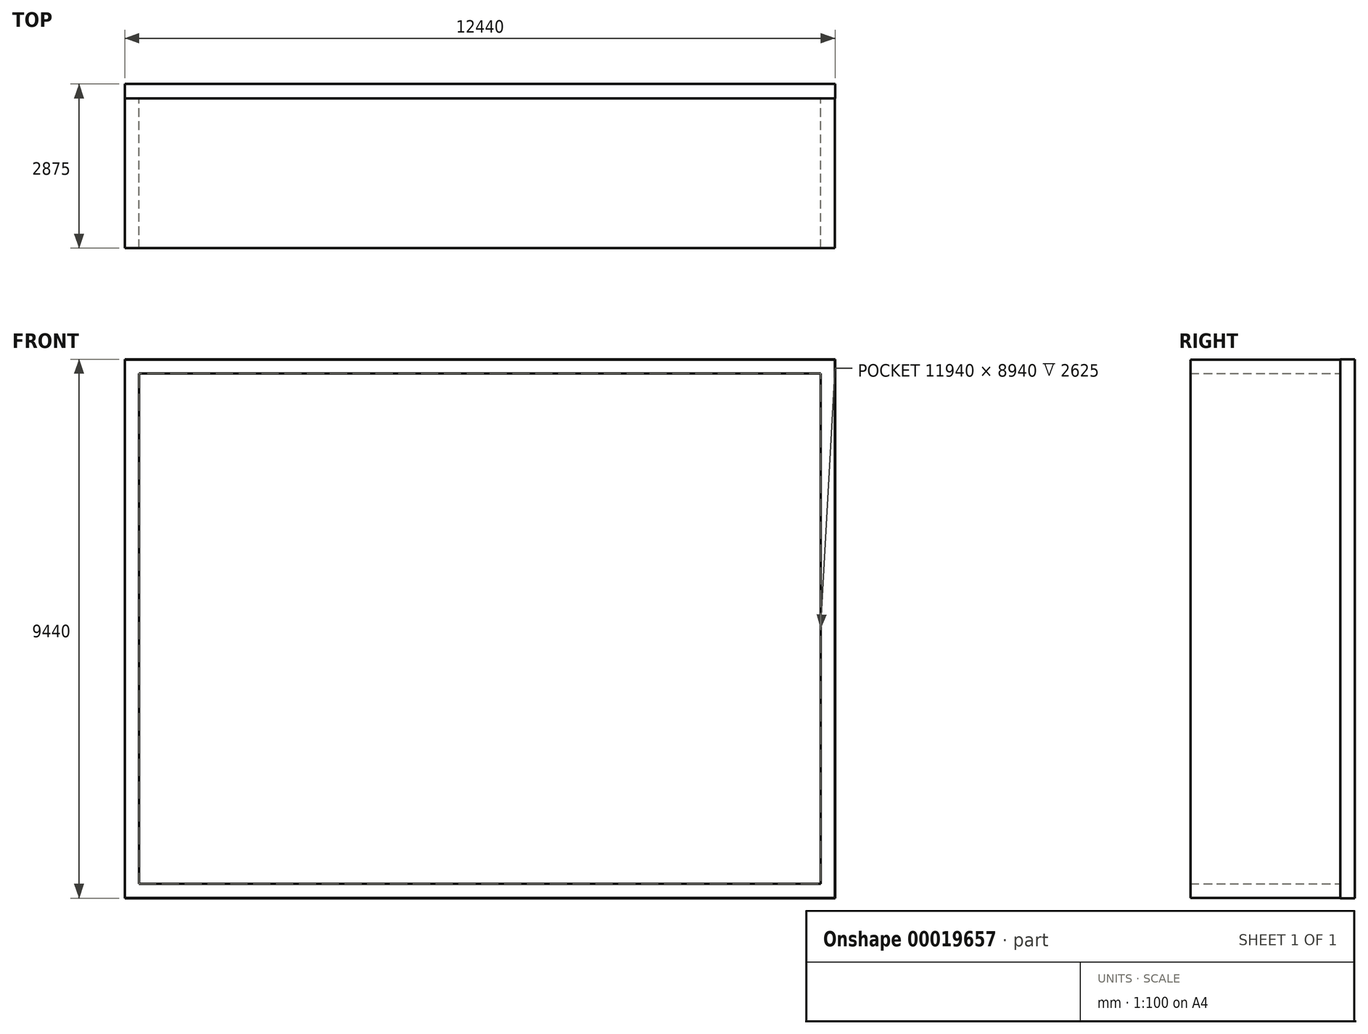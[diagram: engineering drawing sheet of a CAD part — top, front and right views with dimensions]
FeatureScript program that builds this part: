
annotation { "Feature Type Name" : "Feature", "Feature Type Description" : "" }
export const myFeature = defineFeature(function(context is Context, id is Id, definition is map)
    precondition{}
    {
        {
            var Q0;
            Q0=qCreatedBy(makeId("Front.planeOp"),FACE);
            var sketch = newSketch(context, id + "F0", { "sketchPlane" : qUnion([Q0])});
            skLineSegment(sketch, "E0.bottom", {"start": v(0, 0) * mm, "end": v(12440, 0) * mm});
            skLineSegment(sketch, "E0.top", {"start": v(0, 9440) * mm, "end": v(12440, 9440) * mm});
            skLineSegment(sketch, "E0.left", {"start": v(0, 0) * mm, "end": v(0, 9440) * mm});
            skLineSegment(sketch, "E0.right", {"start": v(12440, 0) * mm, "end": v(12440, 9440) * mm});
            skSolve(sketch);
        }
        {
            var Q0;
            Q0=makeQuery(id+"F0.imprint","IMPRINT",FACE,{"disambiguationData":[TD([[makeQuery(id+"F0.imprint","IMPRINT",EDGE,{"derivedFrom":sQuery(id+"F0.wireOp",EDGE,"E0.bottom")}),1.0]])]});
            extrude(context, id + "F1", {"entities" : qUnion([Q0]), "depth" : 250 * mm});
        }
        {
            var Q0;
            Q0=makeQuery(id+"F1.opExtrude","CAP_FACE",FACE,{"disambiguationData":[OSD([sQuery(id+"F0.wireOp",EDGE,"E0.bottom"),sQuery(id+"F0.wireOp",EDGE,"E0.top"),sQuery(id+"F0.wireOp",EDGE,"E0.left"),sQuery(id+"F0.wireOp",EDGE,"E0.right")])],"isStart":false});
            var sketch = newSketch(context, id + "F2", { "sketchPlane" : qUnion([Q0])});
            skLineSegment(sketch, "E1.0.0", {"start": v(0, 9440) * mm, "end": v(0, 0) * mm});
            skLineSegment(sketch, "E1.0.1", {"start": v(0, 0) * mm, "end": v(12440, 0) * mm});
            skLineSegment(sketch, "E1.0.2", {"start": v(12440, 0) * mm, "end": v(12440, 9440) * mm});
            skLineSegment(sketch, "E1.0.3", {"start": v(12440, 9440) * mm, "end": v(0, 9440) * mm});
            skLineSegment(sketch, "E2.0", {"start": v(12190, 9190) * mm, "end": v(250, 9190) * mm});
            skLineSegment(sketch, "E2.1", {"start": v(12190, 250) * mm, "end": v(12190, 9190) * mm});
            skLineSegment(sketch, "E2.2", {"start": v(250, 250) * mm, "end": v(12190, 250) * mm});
            skLineSegment(sketch, "E2.3", {"start": v(250, 9190) * mm, "end": v(250, 250) * mm});
            skLineSegment(sketch, "E3.0", {"start": v(5, 9435) * mm, "end": v(5, 5) * mm});
            skLineSegment(sketch, "E3.1", {"start": v(12435, 9435) * mm, "end": v(5, 9435) * mm});
            skLineSegment(sketch, "E3.2", {"start": v(12435, 5) * mm, "end": v(12435, 9435) * mm});
            skLineSegment(sketch, "E3.3", {"start": v(5, 5) * mm, "end": v(12435, 5) * mm});
            skSolve(sketch);
        }
        {
            var Q0;
            Q0=makeQuery(id+"F2.imprint","IMPRINT",FACE,{"disambiguationData":[TD([[makeQuery(id+"F2.imprint","IMPRINT",EDGE,{"derivedFrom":sQuery(id+"F2.wireOp",EDGE,"E2.0")}),-1.0]])]});
            extrude(context, id + "F3", {"entities" : qUnion([Q0]), "operationType" : NewBodyOperationType.ADD, "depth" : 2625 * mm});
        }
    });
